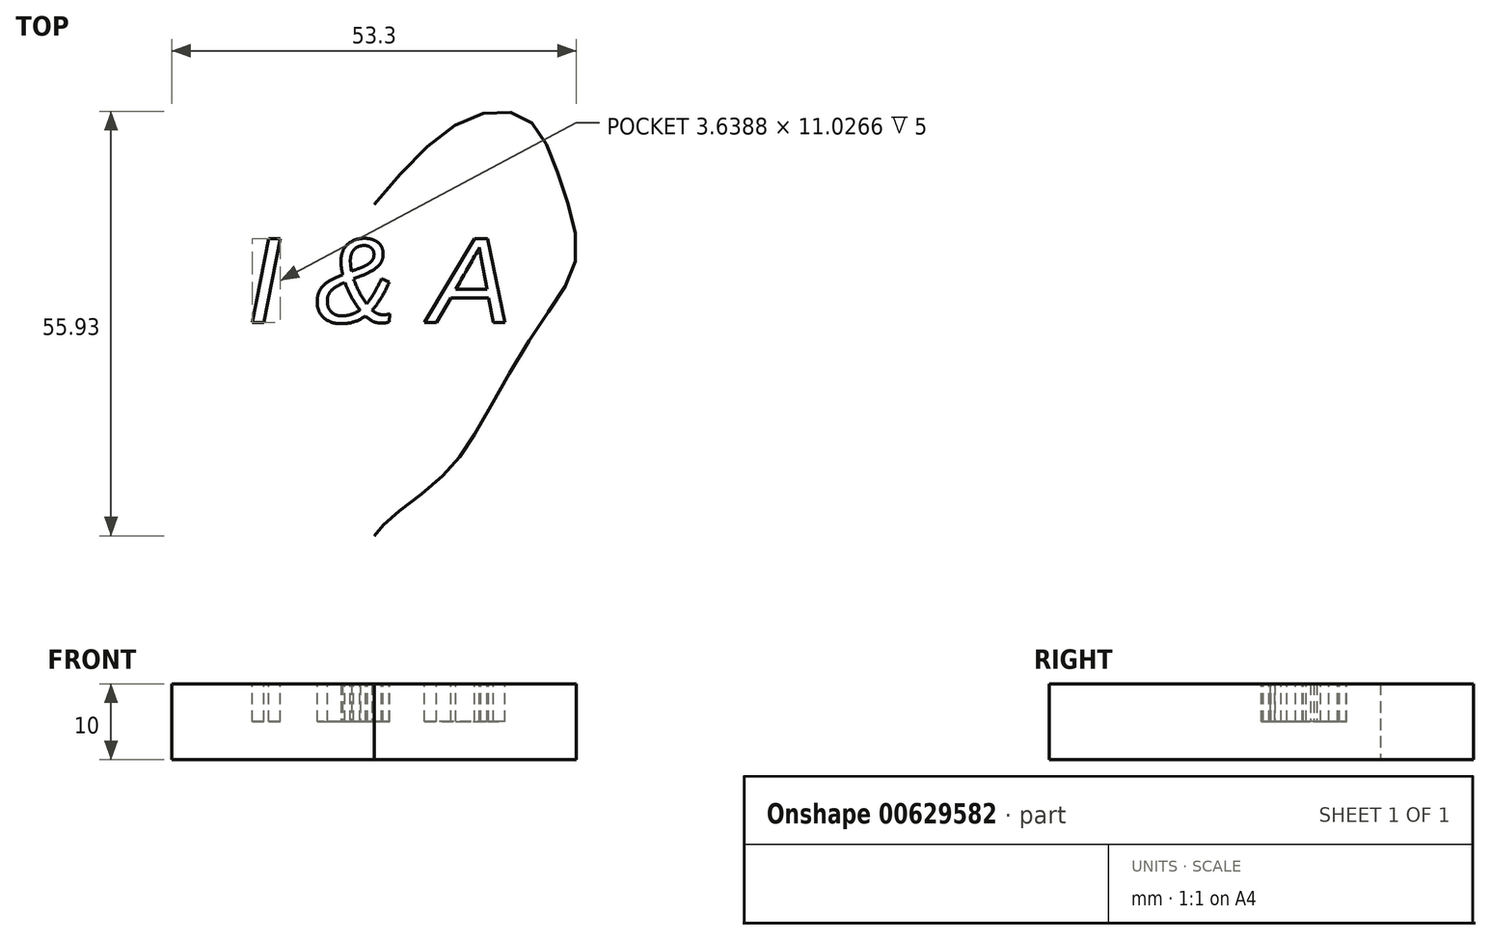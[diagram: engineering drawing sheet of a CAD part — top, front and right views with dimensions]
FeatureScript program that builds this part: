
annotation { "Feature Type Name" : "Feature", "Feature Type Description" : "" }
export const myFeature = defineFeature(function(context is Context, id is Id, definition is map)
    precondition{}
    {
        {
            var Q0;
            Q0=qCreatedBy(makeId("Top.planeOp"),FACE);
            var sketch = newSketch(context, id + "F0", { "sketchPlane" : qUnion([Q0])});
            skFitSpline(sketch, "E0", {"points": [v(0, 13.47) * mm, v(11.89, 24.6) * mm, v(20.06, 24.8) * mm, v(24.33, 17.18) * mm, v(26.56, 6.4) * mm, v(21.54, -2.7) * mm, v(13.56, -16.25) * mm, v(8.54, -22.75) * mm, v(1.86, -28.14) * mm, v(0, -30.18) * mm], "startDerivative": vector(79.58, 94.5) * mm, "endDerivative": vector(-23.82, -31.02) * mm});
            skFitSpline(sketch, "E1.MirrorCS", {"points": [v(0, 13.47) * mm, v(-11.89, 24.6) * mm, v(-20.06, 24.8) * mm, v(-24.33, 17.18) * mm, v(-26.56, 6.4) * mm, v(-21.54, -2.7) * mm, v(-13.56, -16.25) * mm, v(-8.54, -22.75) * mm, v(-1.86, -28.14) * mm, v(0, -30.18) * mm], "startDerivative": vector(-79.58, 94.5) * mm, "endDerivative": vector(23.82, -31.02) * mm});
            skSolve(sketch);
        }
        {
            var Q0;
            Q0 = qSketchRegion(id + "F0", true);
            extrude(context, id + "F1", {"entities" : qUnion([Q0]), "depth" : 10 * mm, "offsetDistance" : 25 * mm});
        }
        {
            var Q0;
            Q0=makeQuery(id+"F1.opExtrude","CAP_FACE",FACE,{"disambiguationData":[OSD([sQuery(id+"F0.wireOp",EDGE,"E0"),sQuery(id+"F0.wireOp",EDGE,"E1.MirrorCS")])],"isStart":false});
            var sketch = newSketch(context, id + "F2", { "sketchPlane" : qUnion([Q0])});
            skText(sketch, "E2", { "text": "I & A", "fontName": "Arimo-Italic.ttf"});
            const initialGuessF2  = {"E2": [-0.01667, -0.00207, 1, 0, 0.01154]};
            skSetInitialGuess(sketch, initialGuessF2);
            skSolve(sketch);
        }
        {
            var Q0;
            Q0 = qSketchRegion(id + "F2", true);
            extrude(context, id + "F3", {"entities" : qUnion([Q0]), "operationType" : NewBodyOperationType.REMOVE, "oppositeDirection" : true, "depth" : 5 * mm, "offsetDistance" : 25 * mm});
        }
    });
